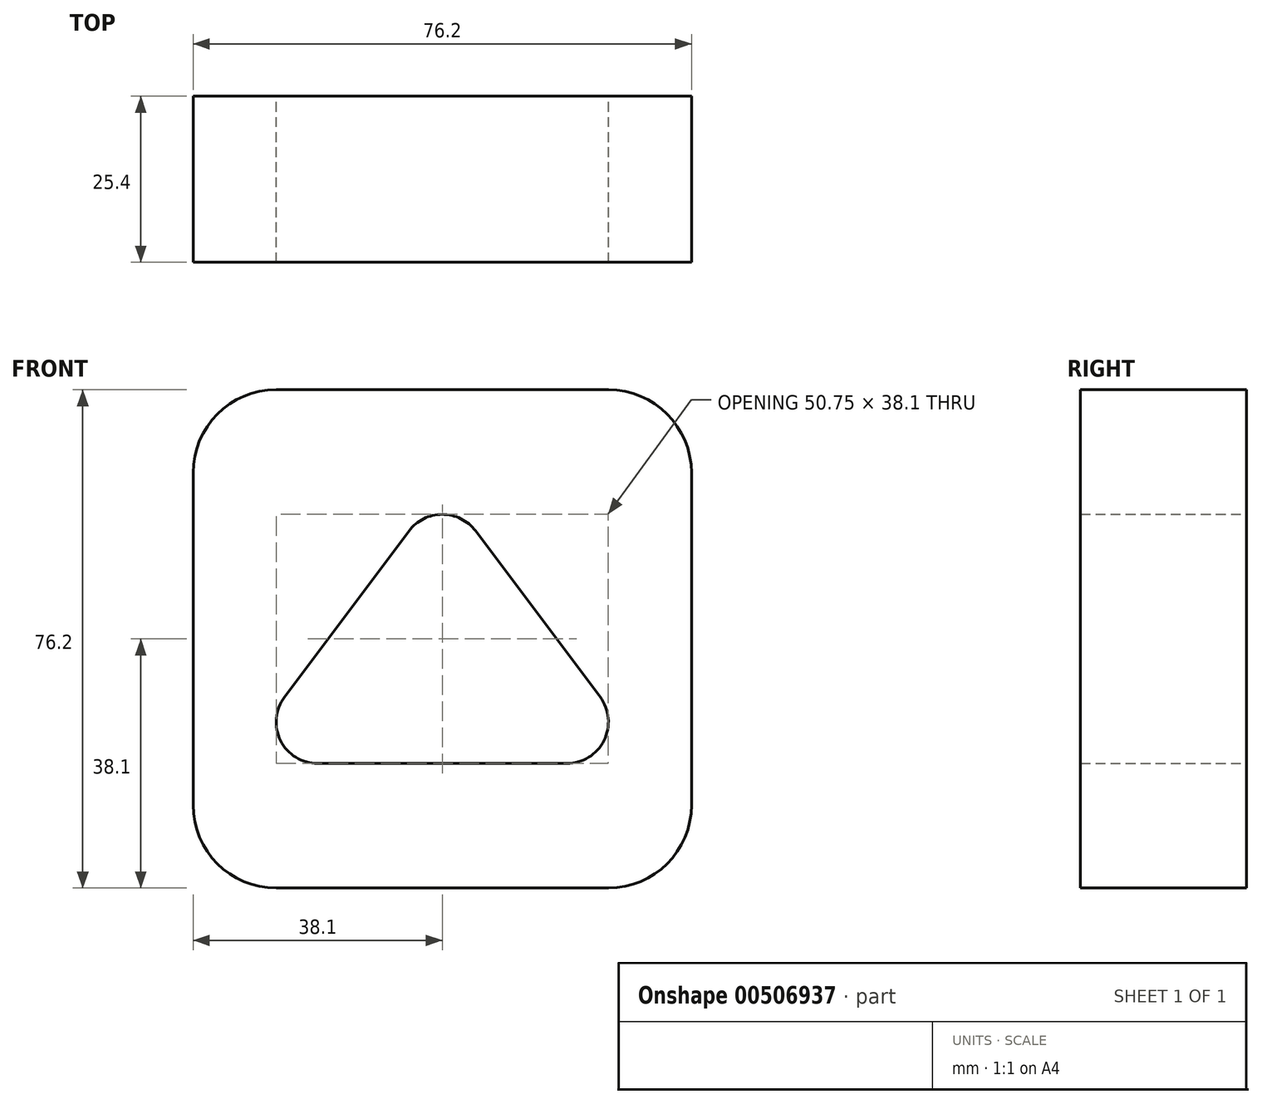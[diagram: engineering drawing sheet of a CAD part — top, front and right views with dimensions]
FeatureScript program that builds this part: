
annotation { "Feature Type Name" : "Feature", "Feature Type Description" : "" }
export const myFeature = defineFeature(function(context is Context, id is Id, definition is map)
    precondition{}
    {
        {
            var Q0;
            Q0=qCreatedBy(makeId("Front.planeOp"),FACE);
            var sketch = newSketch(context, id + "F0", { "sketchPlane" : qUnion([Q0])});
            skLineSegment(sketch, "E0", {"start": v(0, 63.5) * mm, "end": v(0, 12.7) * mm});
            skLineSegment(sketch, "E1", {"start": v(12.7, 0) * mm, "end": v(63.5, 0) * mm});
            skLineSegment(sketch, "E2", {"start": v(76.2, 12.7) * mm, "end": v(76.2, 63.5) * mm});
            skLineSegment(sketch, "E3", {"start": v(63.5, 76.2) * mm, "end": v(12.7, 76.2) * mm});
            skArc(sketch, "E4", {"start": v(13.97, 29.21) * mm, "mid": v(13.37, 22.56) * mm, "end": v(19.05, 19.05) * mm});
            skArc(sketch, "E5", {"start": v(57.15, 19.05) * mm, "mid": v(62.83, 22.56) * mm, "end": v(62.23, 29.21) * mm});
            skArc(sketch, "E6", {"start": v(43.18, 54.6) * mm, "mid": v(38.1, 57.15) * mm, "end": v(33.02, 54.61) * mm});
            skLineSegment(sketch, "E7", {"start": v(33.02, 54.61) * mm, "end": v(13.97, 29.21) * mm});
            skLineSegment(sketch, "E8", {"start": v(43.18, 54.6) * mm, "end": v(62.23, 29.21) * mm});
            skLineSegment(sketch, "E9", {"start": v(57.15, 19.05) * mm, "end": v(19.05, 19.05) * mm});
            skArc(sketch, "E10", {"start": v(0, 12.7) * mm, "mid": v(3.72, 3.72) * mm, "end": v(12.7, 0) * mm});
            skArc(sketch, "E11", {"start": v(12.7, 76.2) * mm, "mid": v(3.72, 72.48) * mm, "end": v(0, 63.5) * mm});
            skPoint(sketch, "E12.orphan", {"position": v(0, 76.2) * mm});
            skArc(sketch, "E13", {"start": v(76.2, 63.5) * mm, "mid": v(72.48, 72.48) * mm, "end": v(63.5, 76.2) * mm});
            skArc(sketch, "E14", {"start": v(63.5, 0) * mm, "mid": v(72.48, 3.72) * mm, "end": v(76.2, 12.7) * mm});
            skSolve(sketch);
        }
        {
            var Q0;
            Q0=makeQuery(id+"F0.imprint","IMPRINT",FACE,{"disambiguationData":[TD([[makeQuery(id+"F0.imprint","IMPRINT",EDGE,{"derivedFrom":sQuery(id+"F0.wireOp",EDGE,"E0")}),1.0]])]});
            extrude(context, id + "F1", {"entities" : qUnion([Q0]), "depth" : 25.4 * mm});
        }
    });
